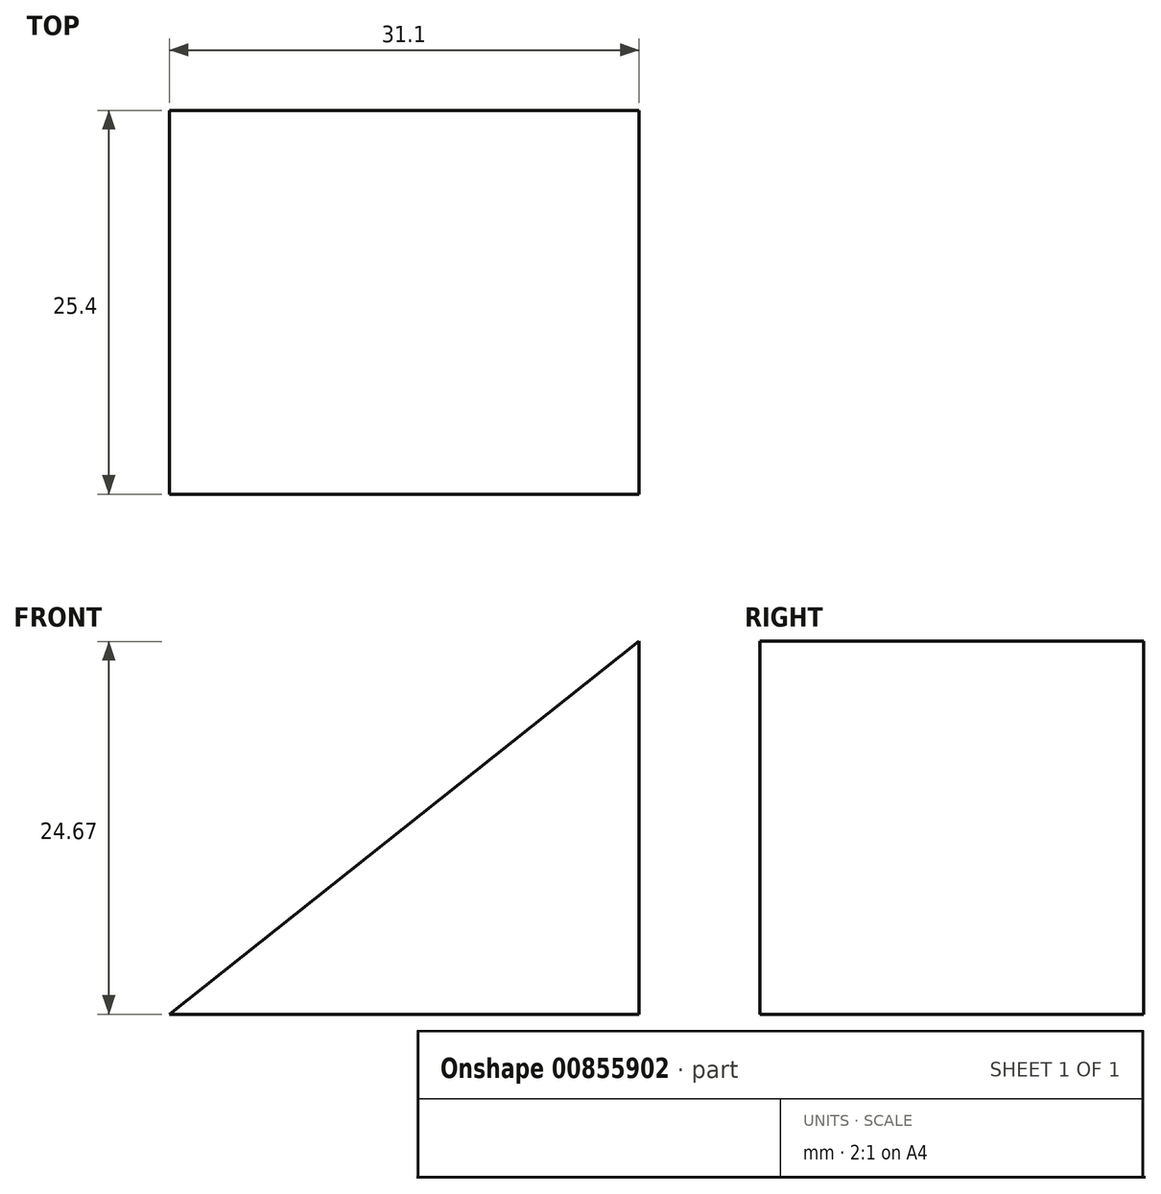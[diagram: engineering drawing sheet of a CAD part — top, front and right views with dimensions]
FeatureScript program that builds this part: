
annotation { "Feature Type Name" : "Feature", "Feature Type Description" : "" }
export const myFeature = defineFeature(function(context is Context, id is Id, definition is map)
    precondition{}
    {
        {
            var Q0;
            Q0=qCreatedBy(makeId("Front.planeOp"),FACE);
            var sketch = newSketch(context, id + "F0", { "sketchPlane" : qUnion([Q0])});
            skLineSegment(sketch, "E0", {"start": v(0, 0) * mm, "end": v(31.1, 0) * mm});
            skLineSegment(sketch, "E1", {"start": v(31.1, 0) * mm, "end": v(31.1, 24.67) * mm});
            skLineSegment(sketch, "E2", {"start": v(31.1, 24.67) * mm, "end": v(0, 0) * mm});
            skSolve(sketch);
        }
        {
            var Q0;
            Q0=makeQuery(id+"F0.imprint","IMPRINT",FACE,{"disambiguationData":[TD([[makeQuery(id+"F0.imprint","IMPRINT",EDGE,{"derivedFrom":sQuery(id+"F0.wireOp",EDGE,"E0")}),1.0]])]});
            extrude(context, id + "F1", {"entities" : qUnion([Q0]), "depth" : 25.4 * mm, "offsetDistance" : 25.4 * mm});
        }
    });
